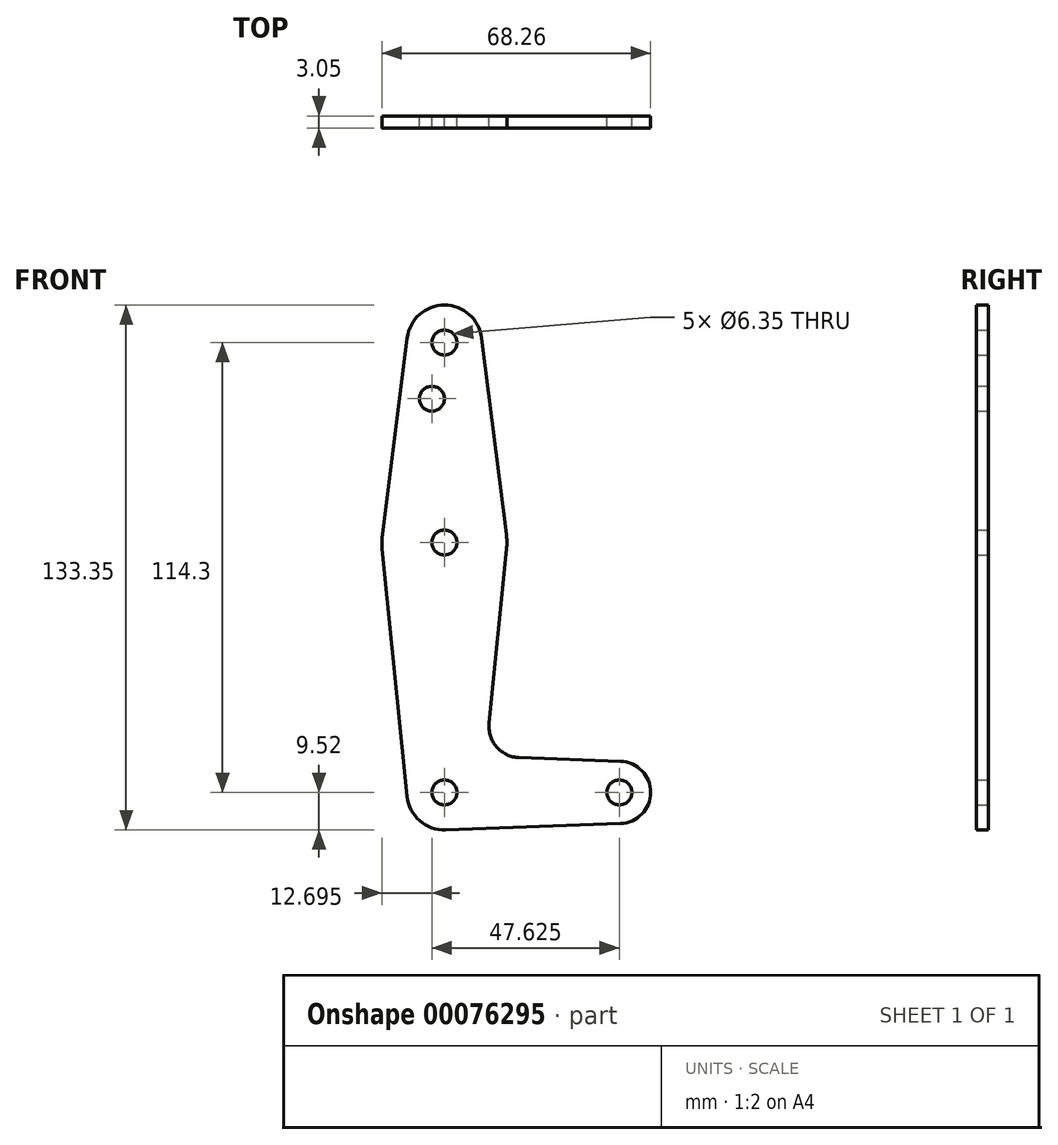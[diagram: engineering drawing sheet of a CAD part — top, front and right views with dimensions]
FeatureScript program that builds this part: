
annotation { "Feature Type Name" : "Feature", "Feature Type Description" : "" }
export const myFeature = defineFeature(function(context is Context, id is Id, definition is map)
    precondition{}
    {
        {
            var Q0;
            Q0=qCreatedBy(makeId("Front.planeOp"),FACE);
            var sketch = newSketch(context, id + "F0", { "sketchPlane" : qUnion([Q0])});
            skCircle(sketch, "E0", {"center": v(0, 114.3) * mm, "radius": 9.53 * mm});
            skCircle(sketch, "E1", {"center": v(0, 63.5) * mm, "radius": 15.88 * mm});
            skCircle(sketch, "E2", {"center": v(0, 0) * mm, "radius": 9.53 * mm});
            skCircle(sketch, "E3", {"center": v(44.45, 0) * mm, "radius": 7.94 * mm});
            skLineSegment(sketch, "E4", {"start": v(0, 0) * mm, "end": v(0, 114.3) * mm, "construction": true});
            skLineSegment(sketch, "E5", {"start": v(0, 0) * mm, "end": v(44.45, 0) * mm, "construction": true});
            skLineSegment(sketch, "E6", {"start": v(-9.45, 115.5) * mm, "end": v(-15.75, 65.48) * mm});
            skLineSegment(sketch, "E7", {"start": v(18.97, 8.85) * mm, "end": v(44.73, 7.93) * mm});
            skLineSegment(sketch, "E8", {"start": v(0.34, -9.52) * mm, "end": v(44.73, -7.93) * mm});
            skLineSegment(sketch, "E9", {"start": v(9.45, 115.5) * mm, "end": v(15.75, 65.48) * mm});
            skCircle(sketch, "E10", {"center": v(0, 114.3) * mm, "radius": 3.18 * mm});
            skCircle(sketch, "E11", {"center": v(-3.18, 100.03) * mm, "radius": 3.18 * mm});
            skCircle(sketch, "E12", {"center": v(0, 63.5) * mm, "radius": 3.18 * mm});
            skCircle(sketch, "E13", {"center": v(0, 0) * mm, "radius": 3.18 * mm});
            skCircle(sketch, "E14", {"center": v(44.45, 0) * mm, "radius": 3.18 * mm});
            skLineSegment(sketch, "E15", {"start": v(-9.48, -0.95) * mm, "end": v(-15.8, 61.91) * mm});
            skLineSegment(sketch, "E16", {"start": v(11.34, 17.6) * mm, "end": v(15.8, 61.91) * mm});
            skArc(sketch, "E17.filletArc", {"start": v(11.34, 17.6) * mm, "mid": v(13.26, 11.57) * mm, "end": v(18.97, 8.85) * mm});
            skSolve(sketch);
        }
        {
            var Q0;
            Q0=makeQuery(id+"F0.imprint","IMPRINT",FACE,{"disambiguationData":[TD([[makeQuery(id+"F0.imprint","IMPRINT",EDGE,{"derivedFrom":sQuery(id+"F0.wireOp",EDGE,"E10")}),-1.0]])]});
            var Q1;
            Q1=makeQuery(id+"F0.imprint","IMPRINT",FACE,{"disambiguationData":[TD([[makeQuery(id+"F0.imprint","IMPRINT",EDGE,{"derivedFrom":sQuery(id+"F0.wireOp",EDGE,"E13")}),-1.0]])]});
            var Q2;
            Q2=makeQuery(id+"F0.imprint","IMPRINT",FACE,{"disambiguationData":[TD([[makeQuery(id+"F0.imprint","IMPRINT",EDGE,{"derivedFrom":sQuery(id+"F0.wireOp",EDGE,"E14")}),-1.0]])]});
            var Q3;
            {var subQ1=sQuery(id+"F0.wireOp",EDGE,"E6");Q3=makeQuery(id+"F0.imprint","IMPRINT",FACE,{"disambiguationData":[TD([[makeQuery(id+"F0.imprint","IMPRINT",EDGE,{"derivedFrom":subQ1}),1.0]])]});}
            var Q4;
            Q4=makeQuery(id+"F0.imprint","IMPRINT",FACE,{"disambiguationData":[TD([[makeQuery(id+"F0.imprint","IMPRINT",EDGE,{"derivedFrom":sQuery(id+"F0.wireOp",EDGE,"E12")}),-1.0]])]});
            var Q5;
            {var subQ0=sQuery(id+"F0.wireOp",EDGE,"E7");Q5=makeQuery(id+"F0.imprint","IMPRINT",FACE,{"disambiguationData":[TD([[makeQuery(id+"F0.imprint","IMPRINT",EDGE,{"derivedFrom":subQ0}),-1.0]])]});}
            extrude(context, id + "F1", {"entities" : qUnion([Q0, Q1, Q2, Q3, Q4, Q5]), "depth" : 3.05 * mm});
        }
    });
